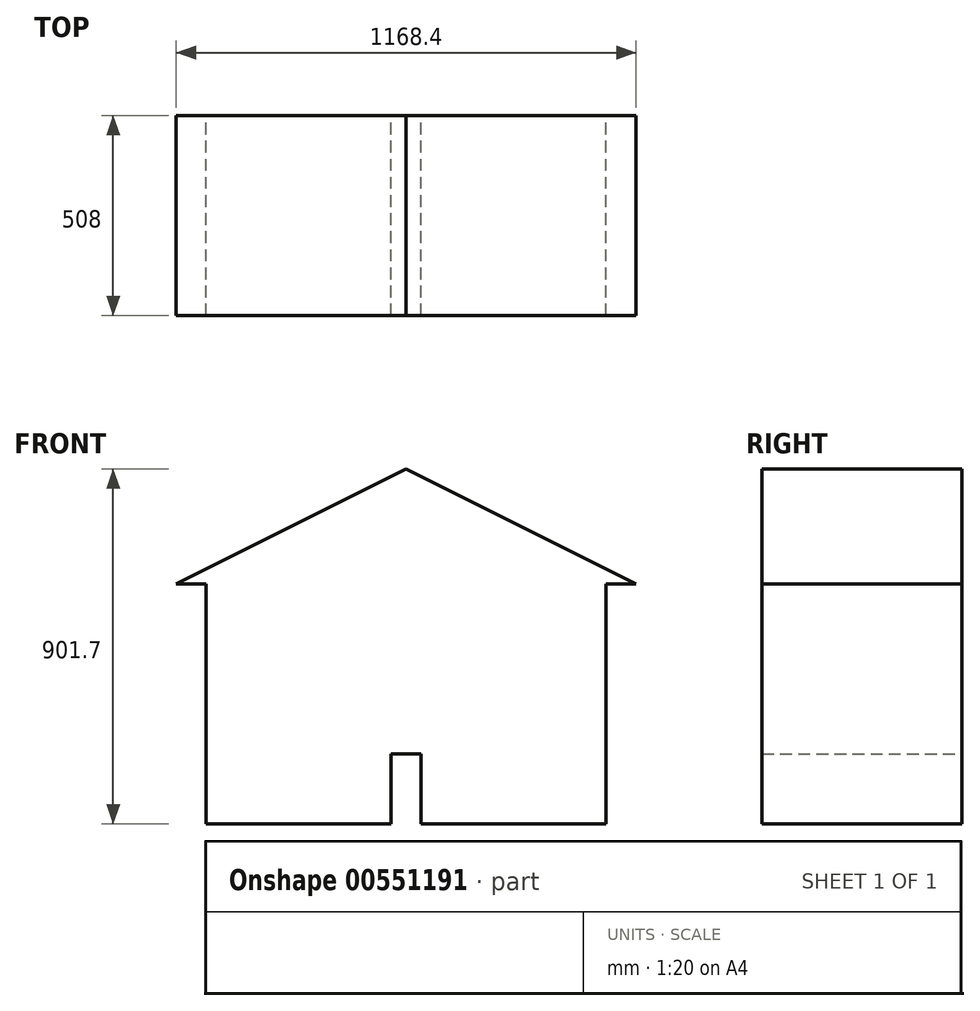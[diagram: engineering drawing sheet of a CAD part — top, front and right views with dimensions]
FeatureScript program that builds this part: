
annotation { "Feature Type Name" : "Feature", "Feature Type Description" : "" }
export const myFeature = defineFeature(function(context is Context, id is Id, definition is map)
    precondition{}
    {
        {
            var Q0;
            Q0=qCreatedBy(makeId("Front.planeOp"),FACE);
            var sketch = newSketch(context, id + "F0", { "sketchPlane" : qUnion([Q0])});
            skLineSegment(sketch, "E0", {"start": v(0, 0) * mm, "end": v(-508, 0) * mm});
            skLineSegment(sketch, "E1", {"start": v(0, 0) * mm, "end": v(508, 0) * mm});
            skLineSegment(sketch, "E2", {"start": v(0, 0) * mm, "end": v(0, 254) * mm, "construction": true});
            skLineSegment(sketch, "E3", {"start": v(-508, 0) * mm, "end": v(0, 254) * mm});
            skLineSegment(sketch, "E4", {"start": v(508, 0) * mm, "end": v(0, 254) * mm});
            skLineSegment(sketch, "E5", {"start": v(-508, 0) * mm, "end": v(-584.2, 0) * mm});
            skLineSegment(sketch, "E6", {"start": v(508, 0) * mm, "end": v(584.2, 0) * mm});
            skLineSegment(sketch, "E7", {"start": v(0, 254) * mm, "end": v(0, 292.1) * mm});
            skLineSegment(sketch, "E8", {"start": v(-584.2, 0) * mm, "end": v(0, 292.1) * mm});
            skLineSegment(sketch, "E9", {"start": v(584.2, 0) * mm, "end": v(0, 292.1) * mm});
            skLineSegment(sketch, "E10", {"start": v(-508, 0) * mm, "end": v(-508, -609.6) * mm});
            skLineSegment(sketch, "E11", {"start": v(-508, -609.6) * mm, "end": v(508, -609.6) * mm});
            skLineSegment(sketch, "E12", {"start": v(508, 0) * mm, "end": v(508, -609.6) * mm});
            skLineSegment(sketch, "E13", {"start": v(0, 0) * mm, "end": v(0, -609.6) * mm, "construction": true});
            skLineSegment(sketch, "E14", {"start": v(0, -609.6) * mm, "end": v(-38.1, -609.6) * mm});
            skLineSegment(sketch, "E15", {"start": v(-38.1, -609.6) * mm, "end": v(-38.1, -431.8) * mm});
            skLineSegment(sketch, "E16", {"start": v(0, -609.6) * mm, "end": v(38.1, -609.6) * mm});
            skLineSegment(sketch, "E17", {"start": v(38.1, -609.6) * mm, "end": v(38.1, -431.8) * mm});
            skLineSegment(sketch, "E18", {"start": v(-38.1, -431.8) * mm, "end": v(38.1, -431.8) * mm});
            skLineSegment(sketch, "E19", {"start": v(-508, -609.6) * mm, "end": v(-508, -635) * mm});
            skLineSegment(sketch, "E20", {"start": v(508, -609.6) * mm, "end": v(508, -635) * mm});
            skLineSegment(sketch, "E21", {"start": v(508, -635) * mm, "end": v(-508, -635) * mm});
            skLineSegment(sketch, "E22.bottom", {"start": v(254, -431.8) * mm, "end": v(431.8, -431.8) * mm});
            skLineSegment(sketch, "E22.top", {"start": v(254, -508) * mm, "end": v(431.8, -508) * mm});
            skLineSegment(sketch, "E22.left", {"start": v(254, -431.8) * mm, "end": v(254, -508) * mm});
            skLineSegment(sketch, "E22.right", {"start": v(431.8, -431.8) * mm, "end": v(431.8, -508) * mm});
            skLineSegment(sketch, "E23.0", {"start": v(228.6, -406.4) * mm, "end": v(457.2, -406.4) * mm});
            skLineSegment(sketch, "E23.1", {"start": v(228.6, -406.4) * mm, "end": v(228.6, -533.4) * mm});
            skLineSegment(sketch, "E23.2", {"start": v(228.6, -533.4) * mm, "end": v(457.2, -533.4) * mm});
            skLineSegment(sketch, "E23.3", {"start": v(457.2, -406.4) * mm, "end": v(457.2, -533.4) * mm});
            skLineSegment(sketch, "E24.bottom", {"start": v(-431.8, -431.8) * mm, "end": v(-254, -431.8) * mm});
            skLineSegment(sketch, "E24.top", {"start": v(-431.8, -508) * mm, "end": v(-254, -508) * mm});
            skLineSegment(sketch, "E24.left", {"start": v(-431.8, -431.8) * mm, "end": v(-431.8, -508) * mm});
            skLineSegment(sketch, "E24.right", {"start": v(-254, -431.8) * mm, "end": v(-254, -508) * mm});
            skLineSegment(sketch, "E25.0", {"start": v(-457.2, -406.4) * mm, "end": v(-228.6, -406.4) * mm});
            skLineSegment(sketch, "E25.1", {"start": v(-457.2, -406.4) * mm, "end": v(-457.2, -533.4) * mm});
            skLineSegment(sketch, "E25.2", {"start": v(-457.2, -533.4) * mm, "end": v(-228.6, -533.4) * mm});
            skLineSegment(sketch, "E25.3", {"start": v(-228.6, -406.4) * mm, "end": v(-228.6, -533.4) * mm});
            skLineSegment(sketch, "E26.bottom", {"start": v(-355.6, -101.6) * mm, "end": v(-101.6, -101.6) * mm});
            skLineSegment(sketch, "E26.top", {"start": v(-355.6, -228.6) * mm, "end": v(-101.6, -228.6) * mm});
            skLineSegment(sketch, "E26.left", {"start": v(-355.6, -101.6) * mm, "end": v(-355.6, -228.6) * mm});
            skLineSegment(sketch, "E26.right", {"start": v(-101.6, -101.6) * mm, "end": v(-101.6, -228.6) * mm});
            skLineSegment(sketch, "E27.0", {"start": v(-381, -76.2) * mm, "end": v(-76.2, -76.2) * mm});
            skLineSegment(sketch, "E27.1", {"start": v(-381, -76.2) * mm, "end": v(-381, -254) * mm});
            skLineSegment(sketch, "E27.2", {"start": v(-381, -254) * mm, "end": v(-76.2, -254) * mm});
            skLineSegment(sketch, "E27.3", {"start": v(-76.2, -76.2) * mm, "end": v(-76.2, -254) * mm});
            skLineSegment(sketch, "E28.bottom", {"start": v(101.6, -101.6) * mm, "end": v(355.6, -101.6) * mm});
            skLineSegment(sketch, "E28.top", {"start": v(101.6, -228.6) * mm, "end": v(355.6, -228.6) * mm});
            skLineSegment(sketch, "E28.left", {"start": v(101.6, -101.6) * mm, "end": v(101.6, -228.6) * mm});
            skLineSegment(sketch, "E28.right", {"start": v(355.6, -101.6) * mm, "end": v(355.6, -228.6) * mm});
            skLineSegment(sketch, "E29.0", {"start": v(76.2, -76.2) * mm, "end": v(381, -76.2) * mm});
            skLineSegment(sketch, "E29.1", {"start": v(76.2, -76.2) * mm, "end": v(76.2, -254) * mm});
            skLineSegment(sketch, "E29.2", {"start": v(76.2, -254) * mm, "end": v(381, -254) * mm});
            skLineSegment(sketch, "E29.3", {"start": v(381, -76.2) * mm, "end": v(381, -254) * mm});
            skLineSegment(sketch, "E30", {"start": v(-508, -211.72) * mm, "end": v(-961.2, -365.8) * mm});
            skLineSegment(sketch, "E31", {"start": v(-961.2, -365.8) * mm, "end": v(-945.44, -626.66) * mm});
            skLineSegment(sketch, "E32", {"start": v(-508, -635) * mm, "end": v(-945.44, -626.66) * mm});
            skLineSegment(sketch, "E33", {"start": v(-508, -234.48) * mm, "end": v(-959.6, -392.27) * mm});
            skLineSegment(sketch, "E34", {"start": v(-508, -609.6) * mm, "end": v(-946.47, -609.6) * mm});
            skLineSegment(sketch, "E35.bottom", {"start": v(-651.3, -411.31) * mm, "end": v(-843.9, -411.31) * mm});
            skLineSegment(sketch, "E35.top", {"start": v(-651.3, -549.63) * mm, "end": v(-843.9, -549.63) * mm});
            skLineSegment(sketch, "E35.left", {"start": v(-651.3, -411.31) * mm, "end": v(-651.3, -549.63) * mm});
            skLineSegment(sketch, "E35.right", {"start": v(-843.9, -411.31) * mm, "end": v(-843.9, -549.63) * mm});
            skLineSegment(sketch, "E36.bottom", {"start": v(-705.58, -462.09) * mm, "end": v(-810.63, -462.09) * mm});
            skLineSegment(sketch, "E36.top", {"start": v(-705.58, -514.61) * mm, "end": v(-810.63, -514.61) * mm});
            skLineSegment(sketch, "E36.left", {"start": v(-705.58, -462.09) * mm, "end": v(-705.58, -514.61) * mm});
            skLineSegment(sketch, "E36.right", {"start": v(-810.63, -462.09) * mm, "end": v(-810.63, -514.61) * mm});
            skSolve(sketch);
        }
        {
            var Q0;
            Q0=makeQuery(id+"F0.imprint","IMPRINT",FACE,{"disambiguationData":[TD([[makeQuery(id+"F0.imprint","IMPRINT",EDGE,{"derivedFrom":sQuery(id+"F0.wireOp",EDGE,"E4")}),-1.0]])]});
            var Q1;
            Q1=makeQuery(id+"F0.imprint","IMPRINT",FACE,{"disambiguationData":[TD([[makeQuery(id+"F0.imprint","IMPRINT",EDGE,{"derivedFrom":sQuery(id+"F0.wireOp",EDGE,"E0")}),-1.0]])]});
            var Q2;
            Q2=makeQuery(id+"F0.imprint","IMPRINT",FACE,{"disambiguationData":[TD([[makeQuery(id+"F0.imprint","IMPRINT",EDGE,{"derivedFrom":sQuery(id+"F0.wireOp",EDGE,"E0")}),1.0]])]});
            var Q3;
            Q3=makeQuery(id+"F0.imprint","IMPRINT",FACE,{"disambiguationData":[TD([[makeQuery(id+"F0.imprint","IMPRINT",EDGE,{"derivedFrom":sQuery(id+"F0.wireOp",EDGE,"E26.bottom")}),-1.0]])]});
            var Q4;
            Q4=makeQuery(id+"F0.imprint","IMPRINT",FACE,{"disambiguationData":[TD([[makeQuery(id+"F0.imprint","IMPRINT",EDGE,{"derivedFrom":sQuery(id+"F0.wireOp",EDGE,"E26.bottom")}),1.0]])]});
            var Q5;
            Q5=makeQuery(id+"F0.imprint","IMPRINT",FACE,{"disambiguationData":[TD([[makeQuery(id+"F0.imprint","IMPRINT",EDGE,{"derivedFrom":sQuery(id+"F0.wireOp",EDGE,"E28.bottom")}),-1.0]])]});
            var Q6;
            Q6=makeQuery(id+"F0.imprint","IMPRINT",FACE,{"disambiguationData":[TD([[makeQuery(id+"F0.imprint","IMPRINT",EDGE,{"derivedFrom":sQuery(id+"F0.wireOp",EDGE,"E28.bottom")}),1.0]])]});
            var Q7;
            Q7=makeQuery(id+"F0.imprint","IMPRINT",FACE,{"disambiguationData":[TD([[makeQuery(id+"F0.imprint","IMPRINT",EDGE,{"derivedFrom":sQuery(id+"F0.wireOp",EDGE,"E24.bottom")}),-1.0]])]});
            var Q8;
            Q8=makeQuery(id+"F0.imprint","IMPRINT",FACE,{"disambiguationData":[TD([[makeQuery(id+"F0.imprint","IMPRINT",EDGE,{"derivedFrom":sQuery(id+"F0.wireOp",EDGE,"E24.bottom")}),1.0]])]});
            var Q9;
            Q9=makeQuery(id+"F0.imprint","IMPRINT",FACE,{"disambiguationData":[TD([[makeQuery(id+"F0.imprint","IMPRINT",EDGE,{"derivedFrom":sQuery(id+"F0.wireOp",EDGE,"E22.bottom")}),1.0]])]});
            var Q10;
            Q10=makeQuery(id+"F0.imprint","IMPRINT",FACE,{"disambiguationData":[TD([[makeQuery(id+"F0.imprint","IMPRINT",EDGE,{"derivedFrom":sQuery(id+"F0.wireOp",EDGE,"E22.bottom")}),-1.0]])]});
            var Q11;
            Q11=makeQuery(id+"F0.imprint","IMPRINT",FACE,{"disambiguationData":[TD([[makeQuery(id+"F0.imprint","IMPRINT",EDGE,{"derivedFrom":sQuery(id+"F0.wireOp",EDGE,"E14")}),-1.0]])]});
            var Q12;
            Q12=makeQuery(id+"F0.imprint","IMPRINT",FACE,{"disambiguationData":[TD([[makeQuery(id+"F0.imprint","IMPRINT",EDGE,{"derivedFrom":sQuery(id+"F0.wireOp",EDGE,"E3")}),1.0]])]});
            extrude(context, id + "F1", {"entities" : qUnion([Q0, Q1, Q2, Q3, Q4, Q5, Q6, Q7, Q8, Q9, Q10, Q11, Q12]), "depth" : 508 * mm, "offsetDistance" : 25.4 * mm});
        }
    });
